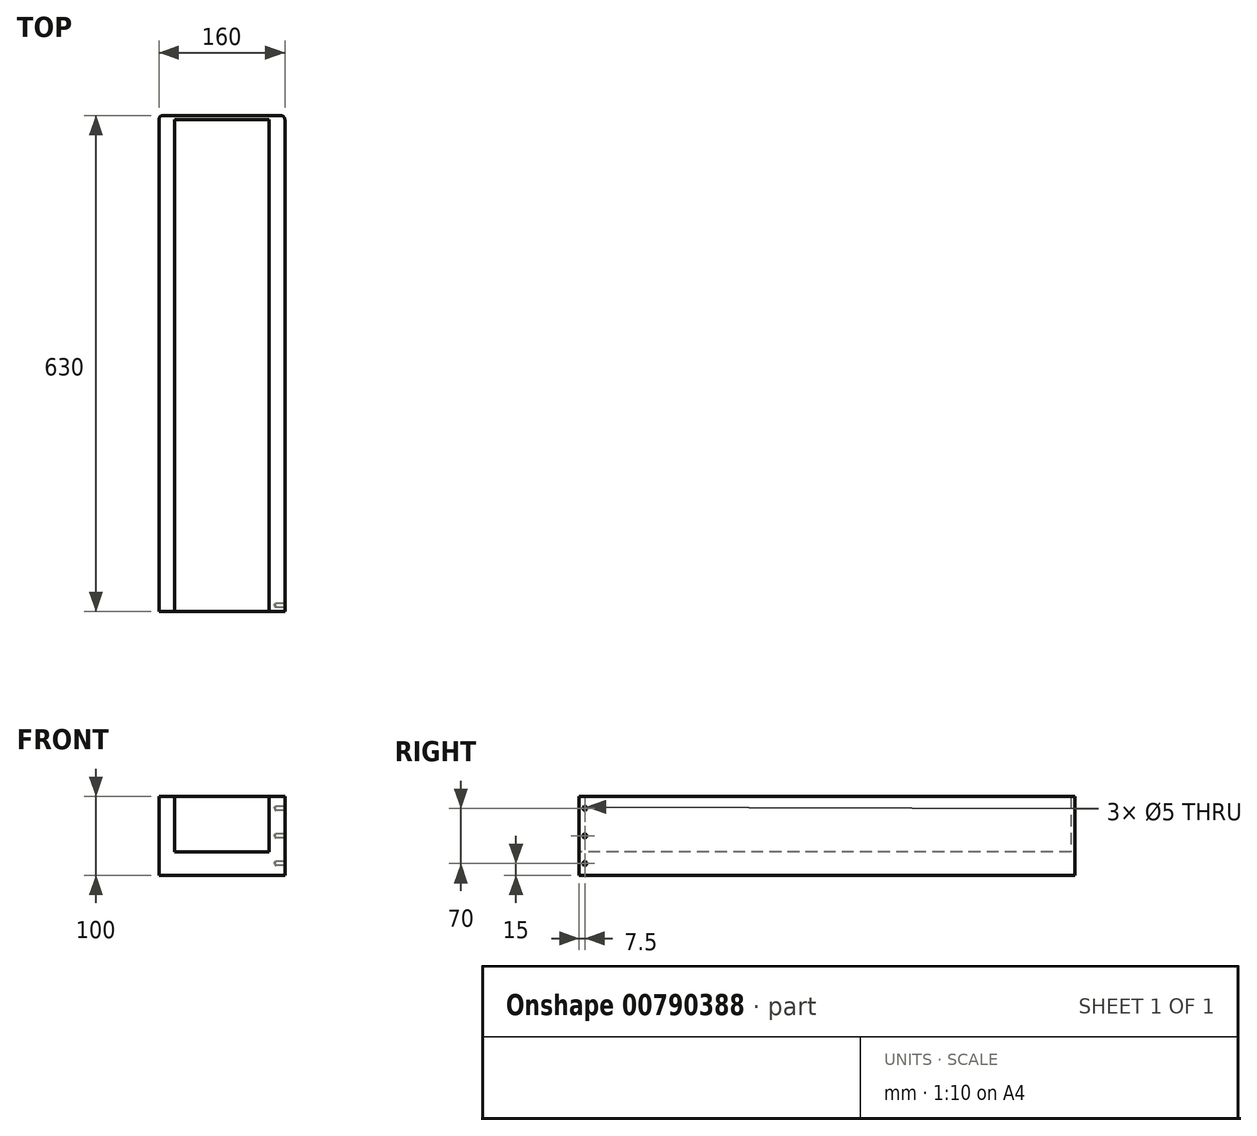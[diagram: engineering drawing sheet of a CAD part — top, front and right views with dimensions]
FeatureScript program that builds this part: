
annotation { "Feature Type Name" : "Feature", "Feature Type Description" : "" }
export const myFeature = defineFeature(function(context is Context, id is Id, definition is map)
    precondition{}
    {
        {
            var Q0;
            Q0=qCreatedBy(makeId("Front.planeOp"),FACE);
            var sketch = newSketch(context, id + "F0", { "sketchPlane" : qUnion([Q0])});
            skLineSegment(sketch, "E0.top", {"start": v(80, 70) * mm, "end": v(60, 70) * mm});
            skLineSegment(sketch, "E0.left", {"start": v(80, -30) * mm, "end": v(80, 70) * mm});
            skLineSegment(sketch, "E0.right", {"start": v(-80, -30) * mm, "end": v(-80, 70) * mm});
            skPoint(sketch, "E0.middle", {"position": v(0, 0) * mm});
            skLineSegment(sketch, "E1.trimOffspring", {"start": v(-60, 70) * mm, "end": v(-80, 70) * mm});
            skLineSegment(sketch, "E2", {"start": v(-80, -30) * mm, "end": v(80, -30) * mm});
            skPoint(sketch, "E3", {"position": v(-70, 55) * mm});
            skPoint(sketch, "E4", {"position": v(70, 55) * mm});
            skPoint(sketch, "E5", {"position": v(70, 20) * mm});
            skPoint(sketch, "E6", {"position": v(-70, 20) * mm});
            skPoint(sketch, "E7", {"position": v(-70, -15) * mm});
            skPoint(sketch, "E8", {"position": v(70, -15) * mm});
            skPoint(sketch, "E9", {"position": v(0, -15) * mm});
            skPoint(sketch, "E10", {"position": v(-70, 70) * mm});
            skPoint(sketch, "E11", {"position": v(70, 70) * mm});
            skLineSegment(sketch, "E12", {"start": v(0, 0) * mm, "end": v(60, 0) * mm});
            skLineSegment(sketch, "E13", {"start": v(60, 70) * mm, "end": v(60, 0) * mm});
            skLineSegment(sketch, "E14", {"start": v(0, 0) * mm, "end": v(-60, 0) * mm});
            skLineSegment(sketch, "E15", {"start": v(-60, 70) * mm, "end": v(-60, 0) * mm});
            skPoint(sketch, "E16.center.orphan", {"position": v(0, 70) * mm});
            skSolve(sketch);
        }
        {
            var Q0;
            Q0=qSketchRegion(id+"F0",true);
            extrude(context, id + "F1", {"entities" : qUnion([Q0]), "oppositeDirection" : true, "depth" : 630 * mm, "offsetDistance" : 25 * mm});
        }
        {
            var Q0;
            Q0=makeQuery(id+"F1.opExtrude","SWEPT_FACE",FACE,{"disambiguationData":[OSD([sQuery(id+"F0.wireOp",EDGE,"E0.left")])]});
            var sketch = newSketch(context, id + "F2", { "sketchPlane" : qUnion([Q0])});
            skPoint(sketch, "E17", {"position": v(7.5, 55) * mm});
            skPoint(sketch, "E18", {"position": v(7.5, 20) * mm});
            skPoint(sketch, "E19", {"position": v(7.5, -15) * mm});
            skSolve(sketch);
        }
        {
            var Q0;
            Q0=sQuery(id+"F2.wireOp",VERTEX,"E17");
            var Q1;
            Q1=sQuery(id+"F2.wireOp",VERTEX,"E18");
            var Q2;
            Q2=sQuery(id+"F2.wireOp",VERTEX,"E19");
            var Q3;
            Q3=makeQuery(id+"F1.opExtrude","SWEPT_BODY",BODY,{"disambiguationData":[OSD([sQuery(id+"F0.wireOp",EDGE,"E0.top"),sQuery(id+"F0.wireOp",EDGE,"E0.left"),sQuery(id+"F0.wireOp",EDGE,"E0.right"),sQuery(id+"F0.wireOp",EDGE,"E1.trimOffspring"),sQuery(id+"F0.wireOp",EDGE,"E2"),sQuery(id+"F0.wireOp",EDGE,"E12"),sQuery(id+"F0.wireOp",EDGE,"E13"),sQuery(id+"F0.wireOp",EDGE,"E14"),sQuery(id+"F0.wireOp",EDGE,"E15")])]});
            hole(context, id + "F3", {"style" : HoleStyle.SIMPLE, "endStyle" : HoleEndStyle.BLIND, "standardTappedOrClearance" : lookupTablePath({ "standard" : "ISO", "engagement" : "75%", "pitch" : "1 mm", "size" : "M6", "type" : "Tapped" }), "standardBlindInLast" : lookupTablePath({ "standard" : "ISO", "engagement" : "75%", "pitch" : "1 mm", "size" : "M6", "type" : "Tapped" }), "holeDiameter" : 5 * mm, "majorDiameter" : 6 * mm, "showTappedDepth" : true, "holeDepth" : 12 * mm, "isTappedThrough" : true, "tappedDepth" : 9 * mm, "tapClearance" : 3, "startFromSketch" : true, "locations" : qUnion([Q0, Q1, Q2]), "scope" : qUnion([Q3])});
        }
        {
            var Q0;
            Q0=makeQuery(id+"F1.opExtrude","CAP_FACE",FACE,{"disambiguationData":[OSD([sQuery(id+"F0.wireOp",EDGE,"E0.top"),sQuery(id+"F0.wireOp",EDGE,"E0.left"),sQuery(id+"F0.wireOp",EDGE,"E0.right"),sQuery(id+"F0.wireOp",EDGE,"E1.trimOffspring"),sQuery(id+"F0.wireOp",EDGE,"E2"),sQuery(id+"F0.wireOp",EDGE,"E12"),sQuery(id+"F0.wireOp",EDGE,"E13"),sQuery(id+"F0.wireOp",EDGE,"E14"),sQuery(id+"F0.wireOp",EDGE,"E15")])],"isStart":false});
            var sketch = newSketch(context, id + "F4", { "sketchPlane" : qUnion([Q0])});
            skLineSegment(sketch, "E20.bottom", {"start": v(-80, 70) * mm, "end": v(80, 70) * mm});
            skLineSegment(sketch, "E20.top", {"start": v(-80, -30) * mm, "end": v(80, -30) * mm});
            skLineSegment(sketch, "E20.left", {"start": v(-80, 70) * mm, "end": v(-80, -30) * mm});
            skLineSegment(sketch, "E20.right", {"start": v(80, 70) * mm, "end": v(80, -30) * mm});
            skSolve(sketch);
        }
        {
            var Q0;
            {var subQ1=makeQuery(id+"F1.opExtrude","CAP_EDGE",EDGE,{"disambiguationData":[OSD([sQuery(id+"F0.wireOp",EDGE,"E13")])],"isStart":false});Q0=makeQuery(id+"F4.imprint","IMPRINT",FACE,{"disambiguationData":[TD([[makeQuery(id+"F4.imprint","IMPRINT",EDGE,{"derivedFrom":subQ1}),1.0]])]});}
            extrude(context, id + "F5", {"entities" : qUnion([Q0]), "operationType" : NewBodyOperationType.ADD, "oppositeDirection" : true, "depth" : 5 * mm, "offsetDistance" : 25 * mm});
        }
        {
            var Q0;
            Q0=makeQuery(id+"F1.opExtrude","SWEPT_FACE",FACE,{"disambiguationData":[OSD([sQuery(id+"F0.wireOp",EDGE,"E12"),sQuery(id+"F0.wireOp",EDGE,"E14")])]});
            var sketch = newSketch(context, id + "F6", { "sketchPlane" : qUnion([Q0])});
            skPoint(sketch, "E21", {"position": v(-20, 555) * mm});
            skPoint(sketch, "E22", {"position": v(20, 555) * mm});
            skPoint(sketch, "E23", {"position": v(-20, 70) * mm});
            skPoint(sketch, "E24", {"position": v(20, 70) * mm});
            skSolve(sketch);
        }
        {
            var Q0;
            Q0=makeQuery(id+"F1.opExtrude","CAP_EDGE",EDGE,{"disambiguationData":[OSD([sQuery(id+"F0.wireOp",EDGE,"E0.right")])],"isStart":false});
            var Q1;
            Q1=makeQuery(id+"F1.opExtrude","CAP_EDGE",EDGE,{"disambiguationData":[OSD([sQuery(id+"F0.wireOp",EDGE,"E0.left")])],"isStart":false});
            fillet(context, id + "F7", {"entities" : qUnion([Q0, Q1]), "radius" : 5 * mm, "tangentPropagation" : true, "allowEdgeOverflow" : false});
        }
    });
